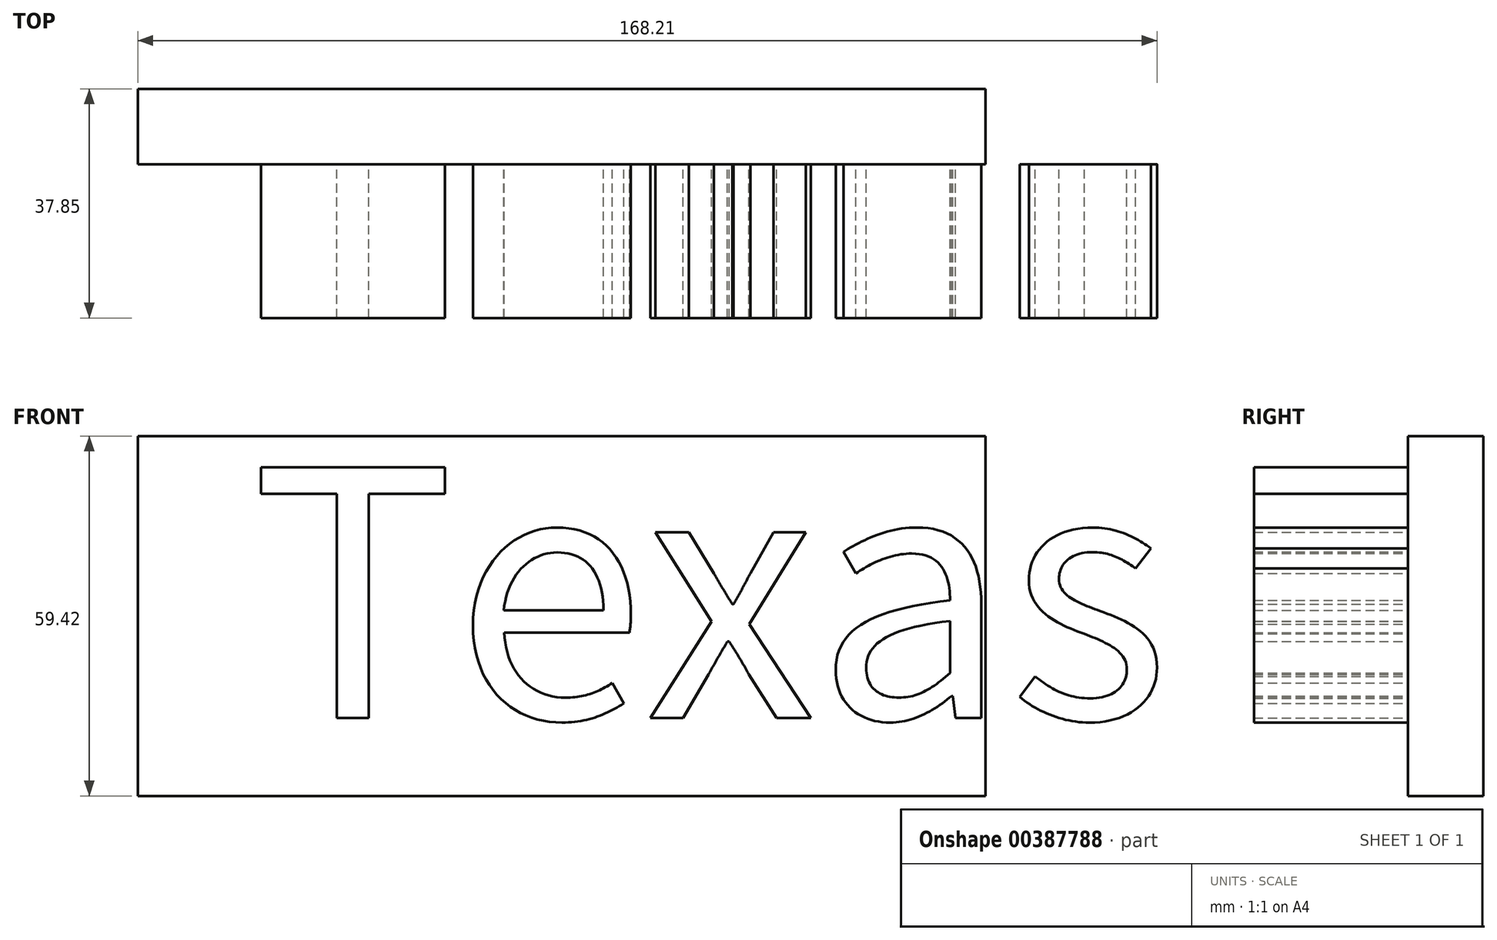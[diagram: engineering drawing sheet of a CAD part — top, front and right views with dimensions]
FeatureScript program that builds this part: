
annotation { "Feature Type Name" : "Feature", "Feature Type Description" : "" }
export const myFeature = defineFeature(function(context is Context, id is Id, definition is map)
    precondition{}
    {
        {
            var Q0;
            Q0=qCreatedBy(makeId("Front.planeOp"),FACE);
            var sketch = newSketch(context, id + "F0", { "sketchPlane" : qUnion([Q0])});
            skLineSegment(sketch, "E0.bottom", {"start": v(-68.4, 46.58) * mm, "end": v(71.5, 46.58) * mm});
            skLineSegment(sketch, "E0.top", {"start": v(-68.4, -12.84) * mm, "end": v(71.5, -12.84) * mm});
            skLineSegment(sketch, "E0.left", {"start": v(-68.4, 46.58) * mm, "end": v(-68.4, -12.84) * mm});
            skLineSegment(sketch, "E0.right", {"start": v(71.5, 46.58) * mm, "end": v(71.5, -12.84) * mm});
            skSolve(sketch);
        }
        {
            var Q0;
            Q0=makeQuery(id+"F0.imprint","IMPRINT",FACE,{"disambiguationData":[TD([[makeQuery(id+"F0.imprint","IMPRINT",EDGE,{"derivedFrom":sQuery(id+"F0.wireOp",EDGE,"E0.bottom")}),-1.0]])]});
            extrude(context, id + "F1", {"entities" : qUnion([Q0]), "depth" : 12.45 * mm});
        }
        {
            var Q0;
            Q0=makeQuery(id+"F1.opExtrude","CAP_FACE",FACE,{"disambiguationData":[OSD([sQuery(id+"F0.wireOp",EDGE,"E0.bottom"),sQuery(id+"F0.wireOp",EDGE,"E0.top"),sQuery(id+"F0.wireOp",EDGE,"E0.left"),sQuery(id+"F0.wireOp",EDGE,"E0.right")])],"isStart":false});
            var sketch = newSketch(context, id + "F2", { "sketchPlane" : qUnion([Q0])});
            skSolve(sketch);
        }
        {
            var Q0;
            Q0=makeQuery(id+"F2.imprint","IMPRINT",FACE,{"disambiguationData":[TD([[makeQuery(id+"F2.imprint","IMPRINT",EDGE,{"derivedFrom":makeQuery(id+"F1.opExtrude","CAP_EDGE",EDGE,{"disambiguationData":[OSD([sQuery(id+"F0.wireOp",EDGE,"E0.bottom")])],"isStart":false})}),-1.0]])]});
            var sketch = newSketch(context, id + "F3", { "sketchPlane" : qUnion([Q0])});
            skText(sketch, "E1", { "text": "Texas", "fontName": "NotoSansCJKtc-Regular.otf"});
            const initialGuessF3  = {"E1": [-0.04983, 0, 1, 0, 0.0407]};
            skSetInitialGuess(sketch, initialGuessF3);
            skSolve(sketch);
        }
        {
            var Q0;
            Q0 = qSketchRegion(id + "F3", true);
            extrude(context, id + "F4", {"entities" : qUnion([Q0]), "operationType" : NewBodyOperationType.ADD, "depth" : 25.4 * mm});
        }
    });
